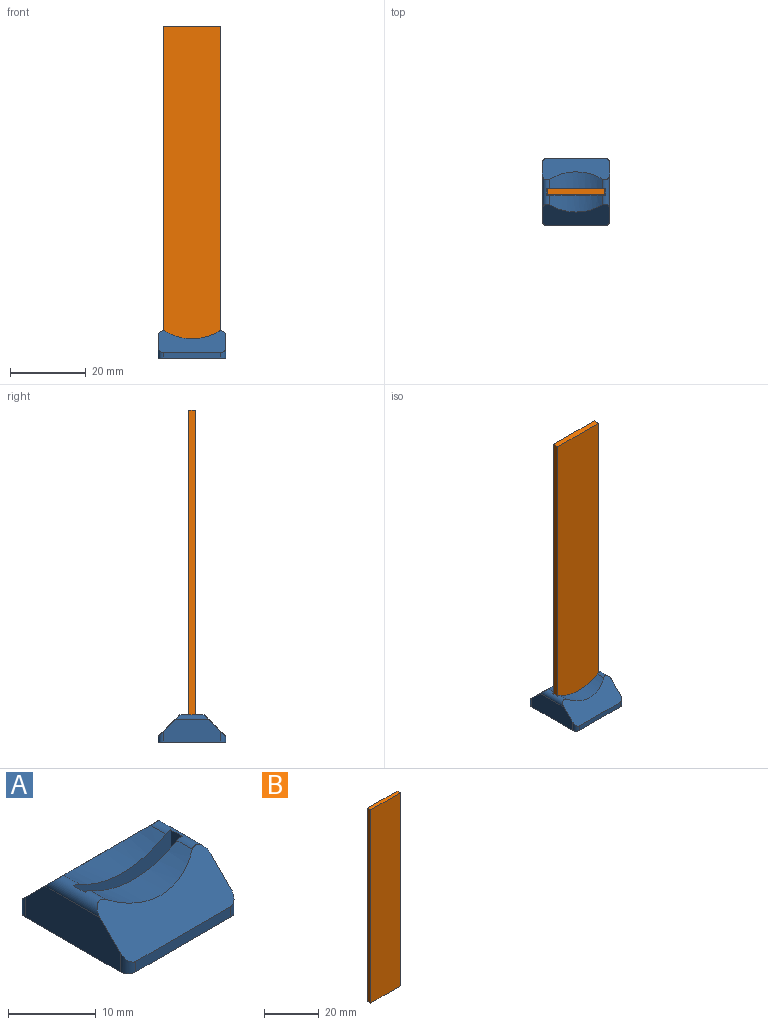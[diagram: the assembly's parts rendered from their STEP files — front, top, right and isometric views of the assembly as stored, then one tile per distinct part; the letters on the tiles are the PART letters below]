
ASSEMBLY  parts=2 mates=1
PART A: 20 faces, bbox 17.8x17.8x7.2 mm
  f0: cylinder r=13.5mm len=13.93mm, axis (0,1,0), area 54.9mm2, adj f10,f12,f14,f15
  f1: plane 15.24x1.45mm, normal (0,-1,0), area 22.1mm2, adj f5,f12,f16,f19
  f2: plane 15.24x5.89mm, normal (1,0,0), area 79.7mm2, adj f5,f12,f13,f14,f16,f17
  f3: plane 15.24x1.45mm, normal (0,1,0), area 22.1mm2, adj f5,f13,f17,f18
  f4: plane 15.24x5.89mm, normal (-1,0,0), area 79.7mm2, adj f5,f12,f13,f15,f18,f19
  f5: plane 17.78x17.78mm, normal (0,0,-1), area 314.7mm2, adj f1,f2,f3,f4,f16,f17,f18,f19
  f6: cylinder r=13.5mm len=13.93mm, axis (0,1,0), area 54.9mm2, adj f8,f13,f14,f15
  f7: plane 15.6x1.8mm, normal (0,0,1), area 28.1mm2, adj f8,f9,f10,f11
  f8: plane 15.6x5.89mm, normal (0,-1,0), area 71mm2, adj f6,f7,f9,f11,f14,f15
  f9: plane 5.87x1.8mm, normal (1,0,0), area 10.6mm2, adj f7,f8,f10,f15
  f10: plane 15.6x5.89mm, normal (0,1,0), area 71mm2, adj f0,f7,f9,f11,f14,f15
  f11: plane 5.87x1.8mm, normal (-1,0,0), area 10.6mm2, adj f7,f8,f10,f14
  f12: plane 17.78x5.71mm, normal (0,-0.71,0.71), area 112.1mm2, adj f0,f1,f2,f4,f14,f15,f16,f19
  f13: plane 17.78x5.71mm, normal (0,0.71,0.71), area 112.1mm2, adj f2,f3,f4,f6,f14,f15,f17,f18
  f14: cylinder r=1.27mm len=8.91mm, axis (0,1,0), area 17.4mm2, adj f0,f2,f6,f8,f10,f11,f12,f13
  f15: cylinder r=1.27mm len=8.91mm, axis (0,1,0), area 17.4mm2, adj f0,f4,f6,f8,f9,f10,f12,f13
  f16: cylinder r=1.27mm len=2.72mm, axis (0,0,1), area 3.8mm2, adj f1,f2,f5,f12
  f17: cylinder r=1.27mm len=2.72mm, axis (0,0,-1), area 3.8mm2, adj f2,f3,f5,f13
  f18: cylinder r=1.27mm len=2.72mm, axis (0,0,1), area 3.8mm2, adj f3,f4,f5,f13
  f19: cylinder r=1.27mm len=2.72mm, axis (0,0,-1), area 3.8mm2, adj f1,f4,f5,f12
PART B: 6 faces, bbox 15.2x1.6x86.4 mm
  f0: plane 15.24x1.6mm, normal (0,0,-1), area 24.4mm2, adj f1,f3,f4,f5
  f1: plane 86.36x1.6mm, normal (1,0,0), area 138.2mm2, adj f0,f2,f4,f5
  f2: plane 15.24x1.6mm, normal (0,0,1), area 24.4mm2, adj f1,f3,f4,f5
  f3: plane 86.36x1.6mm, normal (-1,0,0), area 138.2mm2, adj f0,f2,f4,f5
  f4: plane 86.36x15.24mm, normal (0,-1,0), area 1316.1mm2, adj f0,f1,f2,f3
  f5: plane 86.36x15.24mm, normal (0,1,0), area 1316.1mm2, adj f0,f1,f2,f3
PLACE A t=(2.42,16.78,0.16)mm
PLACE B t=(2.42,17.58,44.61)mm
MATE fastened A.f7 <-> B.f0  axis (0,0,1) through (2.42,16.78,1.43)mm
